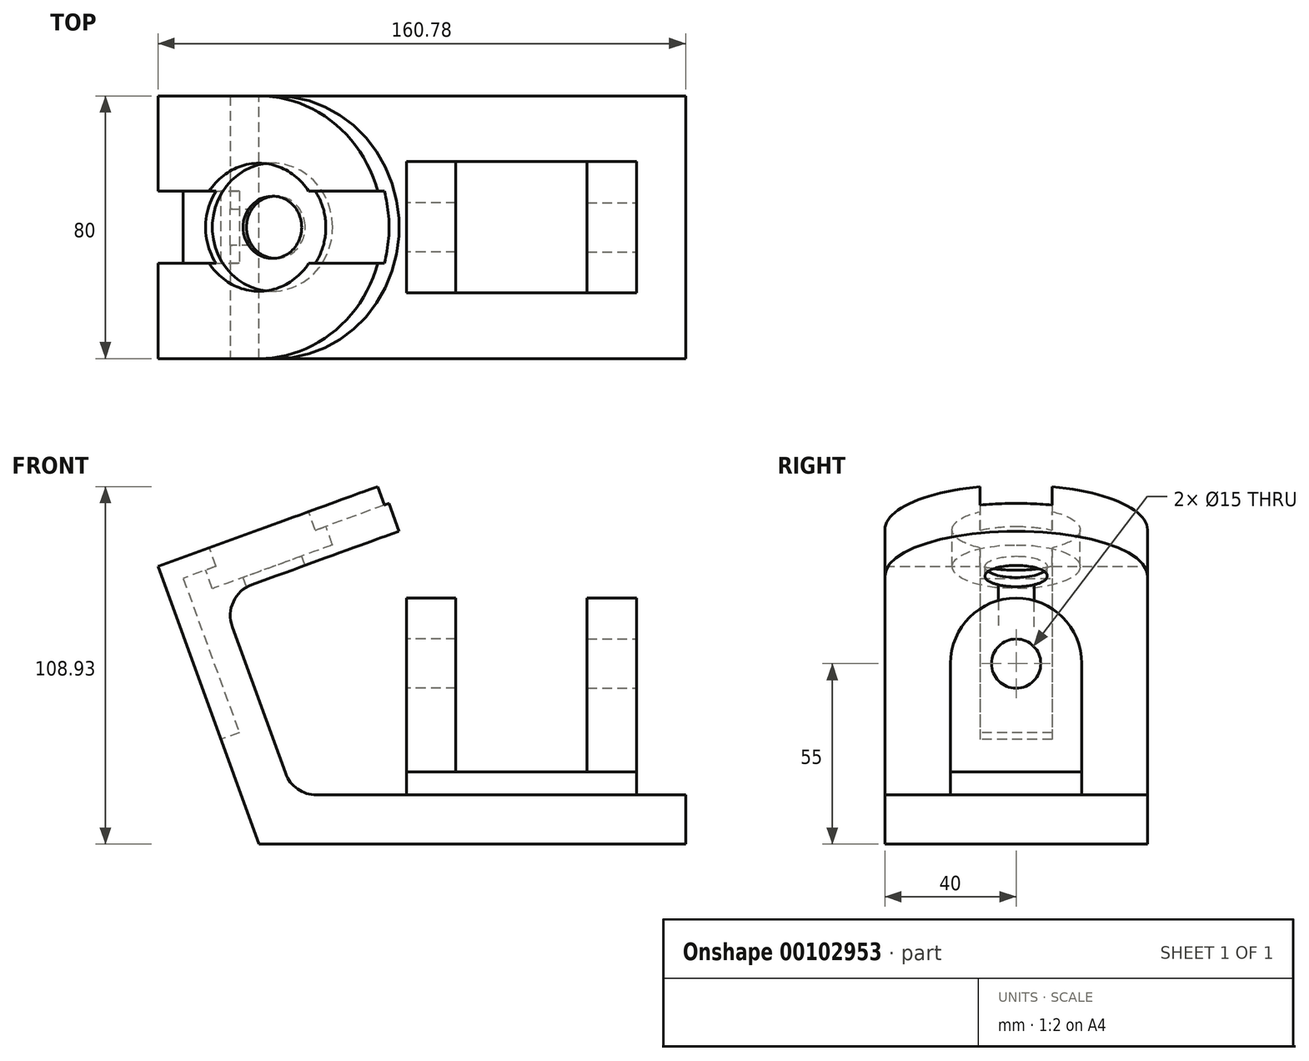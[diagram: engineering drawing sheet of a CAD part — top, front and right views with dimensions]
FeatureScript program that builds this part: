
annotation { "Feature Type Name" : "Feature", "Feature Type Description" : "" }
export const myFeature = defineFeature(function(context is Context, id is Id, definition is map)
    precondition{}
    {
        {
            var Q0;
            Q0=qCreatedBy(makeId("Front.planeOp"),FACE);
            var sketch = newSketch(context, id + "F0", { "sketchPlane" : qUnion([Q0])});
            skLineSegment(sketch, "E0", {"start": v(0, 0) * mm, "end": v(130, 0) * mm});
            skLineSegment(sketch, "E1", {"start": v(130, 0) * mm, "end": v(130, 15) * mm});
            skLineSegment(sketch, "E2", {"start": v(130, 15) * mm, "end": v(10.5, 15) * mm});
            skLineSegment(sketch, "E3", {"start": v(10.5, 15) * mm, "end": v(-11.56, 75.6) * mm});
            skLineSegment(sketch, "E4", {"start": v(-11.56, 75.6) * mm, "end": v(5.13, 81.68) * mm});
            skLineSegment(sketch, "E5", {"start": v(5.13, 81.68) * mm, "end": v(0, 95.78) * mm});
            skLineSegment(sketch, "E6", {"start": v(0, 95.78) * mm, "end": v(-30.78, 84.57) * mm});
            skLineSegment(sketch, "E7", {"start": v(-30.78, 84.57) * mm, "end": v(0, 0) * mm});
            skSolve(sketch);
        }
        {
            var Q0;
            Q0=makeQuery(id+"F0.imprint","IMPRINT",FACE,{"disambiguationData":[TD([[makeQuery(id+"F0.imprint","IMPRINT",EDGE,{"derivedFrom":sQuery(id+"F0.wireOp",EDGE,"E0")}),1.0]])]});
            extrude(context, id + "F1", {"entities" : qUnion([Q0]), "depth" : 80 * mm});
        }
        {
            var Q0;
            Q0=makeQuery(id+"F1.opExtrude","SWEPT_FACE",FACE,{"disambiguationData":[OSD([sQuery(id+"F0.wireOp",EDGE,"E6")])]});
            var sketch = newSketch(context, id + "F2", { "sketchPlane" : qUnion([Q0])});
            skArc(sketch, "E8", {"start": v(32.76, -80) * mm, "mid": v(72.76, -40) * mm, "end": v(32.76, 0) * mm});
            skCircle(sketch, "E9", {"center": v(32.76, -40) * mm, "radius": 9.5 * mm});
            skSolve(sketch);
        }
        {
            var Q0;
            {var subQ0=sQuery(id+"F2.wireOp",EDGE,"E8");Q0=makeQuery(id+"F2.imprint","IMPRINT",FACE,{"disambiguationData":[TD([[makeQuery(id+"F2.imprint","IMPRINT",EDGE,{"derivedFrom":subQ0}),1.0]])]});}
            extrude(context, id + "F3", {"entities" : qUnion([Q0]), "operationType" : NewBodyOperationType.ADD, "oppositeDirection" : true, "depth" : 15 * mm});
        }
        {
            var Q0;
            Q0=makeQuery(id+"F1.opExtrude","SWEPT_FACE",FACE,{"disambiguationData":[OSD([sQuery(id+"F0.wireOp",EDGE,"E6")])]});
            var sketch = newSketch(context, id + "F4", { "sketchPlane" : qUnion([Q0])});
            skCircle(sketch, "E10", {"center": v(32.76, -40) * mm, "radius": 9.5 * mm});
            skSolve(sketch);
        }
        {
            var Q0;
            {var subQ1=makeQuery(id+"F1.opExtrude","SWEPT_EDGE",EDGE,{"disambiguationData":[OSD([sQuery(id+"F0.wireOp",EDGE,"E5"),sQuery(id+"F0.wireOp",EDGE,"E6")])]});Q0=makeQuery(id+"F4.imprint","IMPRINT",FACE,{"disambiguationData":[TD([[makeQuery(id+"F4.imprint","IMPRINT",EDGE,{"derivedFrom":subQ1}),1.0]])]});}
            extrude(context, id + "F5", {"entities" : qUnion([Q0]), "operationType" : NewBodyOperationType.REMOVE, "oppositeDirection" : true, "depth" : 15 * mm});
        }
        {
            var Q0;
            Q0=makeQuery(id+"F1.opExtrude","SWEPT_FACE",FACE,{"disambiguationData":[OSD([sQuery(id+"F0.wireOp",EDGE,"E2")])]});
            var sketch = newSketch(context, id + "F6", { "sketchPlane" : qUnion([Q0])});
            skLineSegment(sketch, "E11.bottom", {"start": v(45, -20) * mm, "end": v(115, -20) * mm});
            skLineSegment(sketch, "E11.top", {"start": v(45, -60) * mm, "end": v(115, -60) * mm});
            skLineSegment(sketch, "E11.left", {"start": v(45, -20) * mm, "end": v(45, -60) * mm});
            skLineSegment(sketch, "E11.right", {"start": v(115, -20) * mm, "end": v(115, -60) * mm});
            skLineSegment(sketch, "E12", {"start": v(115, -40) * mm, "end": v(130, -40) * mm, "construction": true});
            skSolve(sketch);
        }
        {
            var Q0;
            Q0=makeQuery(id+"F6.imprint","IMPRINT",FACE,{"disambiguationData":[TD([[makeQuery(id+"F6.imprint","IMPRINT",EDGE,{"derivedFrom":sQuery(id+"F6.wireOp",EDGE,"E11.bottom")}),-1.0]])]});
            extrude(context, id + "F7", {"entities" : qUnion([Q0]), "operationType" : NewBodyOperationType.ADD, "depth" : 7 * mm});
        }
        {
            var Q0;
            Q0=makeQuery(id+"F7.opExtrude","SWEPT_FACE",FACE,{"disambiguationData":[OSD([sQuery(id+"F6.wireOp",EDGE,"E11.right")])]});
            var sketch = newSketch(context, id + "F8", { "sketchPlane" : qUnion([Q0])});
            skLineSegment(sketch, "E13.bottom", {"start": v(-60, 22) * mm, "end": v(-20, 22) * mm});
            skLineSegment(sketch, "E13.top", {"start": v(-60, 55) * mm, "end": v(-20, 55) * mm});
            skLineSegment(sketch, "E13.left", {"start": v(-60, 22) * mm, "end": v(-60, 55) * mm});
            skLineSegment(sketch, "E13.right", {"start": v(-20, 22) * mm, "end": v(-20, 55) * mm});
            skArc(sketch, "E14", {"start": v(-20, 55) * mm, "mid": v(-40, 75) * mm, "end": v(-60, 55) * mm});
            skCircle(sketch, "E15", {"center": v(-40, 55) * mm, "radius": 7.5 * mm});
            skSolve(sketch);
        }
        {
            var Q0;
            Q0 = qSketchRegion(id + "F8", true);
            extrude(context, id + "F9", {"entities" : qUnion([Q0]), "oppositeDirection" : true, "depth" : 15 * mm});
        }
        {
            var Q0;
            Q0=makeQuery(id+"F7.opExtrude","SWEPT_FACE",FACE,{"disambiguationData":[OSD([sQuery(id+"F6.wireOp",EDGE,"E11.left")])]});
            cPlane(context, id + "F10", {"entities" : qUnion([Q0]), "cplaneType" : CPlaneType.OFFSET, "offset" : 35 * mm, "oppositeDirection" : true, "width" : 150 * mm, "height" : 150 * mm});
        }
        {
            var Q0;
            Q0=makeQuery(id+"F9.opExtrude","SWEPT_BODY",BODY,{"disambiguationData":[OSD([sQuery(id+"F8.wireOp",EDGE,"E13.bottom"),sQuery(id+"F8.wireOp",EDGE,"E13.left"),sQuery(id+"F8.wireOp",EDGE,"E13.right"),sQuery(id+"F8.wireOp",EDGE,"E14"),sQuery(id+"F8.wireOp",EDGE,"E15")])]});
            var Q1;
            Q1=qCreatedBy(id+"F10.planeOp",FACE);
            mirror(context, id + "F11", {"entities" : qUnion([Q0]), "mirrorPlane" : qUnion([Q1])});
        }
        {
            var Q0;
            Q0=makeQuery(id+"F1.opExtrude","SWEPT_FACE",FACE,{"disambiguationData":[OSD([sQuery(id+"F0.wireOp",EDGE,"E7")])]});
            var sketch = newSketch(context, id + "F12", { "sketchPlane" : qUnion([Q0])});
            skLineSegment(sketch, "E16.bottom", {"start": v(29, 90) * mm, "end": v(51, 90) * mm});
            skLineSegment(sketch, "E16.top", {"start": v(29, 34) * mm, "end": v(51, 34) * mm});
            skLineSegment(sketch, "E16.left", {"start": v(29, 90) * mm, "end": v(29, 34) * mm});
            skLineSegment(sketch, "E16.right", {"start": v(51, 90) * mm, "end": v(51, 34) * mm});
            skLineSegment(sketch, "E17", {"start": v(40, 90) * mm, "end": v(40, 34) * mm, "construction": true});
            skSolve(sketch);
        }
        {
            var Q0;
            Q0=makeQuery(id+"F12.imprint","IMPRINT",FACE,{"disambiguationData":[TD([[makeQuery(id+"F12.imprint","IMPRINT",EDGE,{"derivedFrom":sQuery(id+"F12.wireOp",EDGE,"E16.bottom")}),1.0]])]});
            extrude(context, id + "F13", {"entities" : qUnion([Q0]), "operationType" : NewBodyOperationType.REMOVE, "oppositeDirection" : true, "depth" : 6 * mm});
        }
        {
            var Q0;
            {var subQ1=sQuery(id+"F2.wireOp",EDGE,"E8");var subQ2=sQuery(id+"F0.wireOp",EDGE,"E6");var subQ3=sQuery(id+"F0.wireOp",EDGE,"E5");Q0=makeQuery(id+"F16.boolean.opBoolean","SPLIT",FACE,{"disambiguationData":[TD([makeQuery(id+"F13.boolean.opBoolean","COPY",FACE,{"derivedFrom":makeQuery(id+"F13.opExtrude","SWEPT_FACE",FACE,{"disambiguationData":[OSD([sQuery(id+"F12.wireOp",EDGE,"E16.left")])]})})])],"derivedFrom":makeQuery(id+"F3.boolean.opBoolean","MERGE",FACE,{"derivedFrom":[makeQuery(id+"F1.opExtrude","SWEPT_FACE",FACE,{"disambiguationData":[OSD([subQ2])]}),makeQuery(id+"F3.opExtrude","CAP_FACE",FACE,{"disambiguationData":[OSD([subQ3,subQ2,subQ1,sQuery(id+"F2.wireOp",EDGE,"E9")])],"isStart":true})]})});}
            var sketch = newSketch(context, id + "F14", { "sketchPlane" : qUnion([Q0])});
            skCircle(sketch, "E18", {"center": v(32.76, -40) * mm, "radius": 19.5 * mm});
            skSolve(sketch);
        }
        {
            var Q0;
            {var subQ0=sQuery(id+"F0.wireOp",EDGE,"E6");Q0=makeQuery(id+"F3.boolean.opBoolean","MERGE",FACE,{"derivedFrom":[makeQuery(id+"F1.opExtrude","SWEPT_FACE",FACE,{"disambiguationData":[OSD([subQ0])]}),makeQuery(id+"F3.opExtrude","CAP_FACE",FACE,{"disambiguationData":[OSD([sQuery(id+"F0.wireOp",EDGE,"E5"),subQ0,sQuery(id+"F2.wireOp",EDGE,"E8"),sQuery(id+"F2.wireOp",EDGE,"E9")])],"isStart":true})]});}
            var sketch = newSketch(context, id + "F15", { "sketchPlane" : qUnion([Q0])});
            skLineSegment(sketch, "E19.bottom", {"start": v(0, -29) * mm, "end": v(72.76, -29) * mm});
            skLineSegment(sketch, "E19.top", {"start": v(0, -51) * mm, "end": v(72.76, -51) * mm});
            skLineSegment(sketch, "E19.left", {"start": v(0, -29) * mm, "end": v(0, -51) * mm});
            skLineSegment(sketch, "E19.right", {"start": v(72.76, -29) * mm, "end": v(72.76, -51) * mm});
            skSolve(sketch);
        }
        {
            var Q0;
            Q0 = qSketchRegion(id + "F15", true);
            extrude(context, id + "F16", {"entities" : qUnion([Q0]), "operationType" : NewBodyOperationType.REMOVE, "oppositeDirection" : true, "depth" : 6 * mm});
        }
        {
            var Q0;
            Q0=makeQuery(id+"F14.imprint","IMPRINT",FACE,{"disambiguationData":[TD([[makeQuery(id+"F14.imprint","IMPRINT",EDGE,{"derivedFrom":sQuery(id+"F14.wireOp",EDGE,"E18")}),1.0]])]});
            extrude(context, id + "F17", {"entities" : qUnion([Q0]), "operationType" : NewBodyOperationType.REMOVE, "oppositeDirection" : true, "depth" : 12 * mm});
        }
        {
            var Q0;
            Q0=makeQuery(id+"F1.opExtrude","SWEPT_EDGE",EDGE,{"disambiguationData":[OSD([sQuery(id+"F0.wireOp",EDGE,"E3"),sQuery(id+"F0.wireOp",EDGE,"E4")])]});
            var Q1;
            Q1=makeQuery(id+"F1.opExtrude","SWEPT_EDGE",EDGE,{"disambiguationData":[OSD([sQuery(id+"F0.wireOp",EDGE,"E2"),sQuery(id+"F0.wireOp",EDGE,"E3")])]});
            fillet(context, id + "F18", {"entities" : qUnion([Q0, Q1]), "radius" : 10 * mm, "tangentPropagation" : true, "allowEdgeOverflow" : false});
        }
    });
